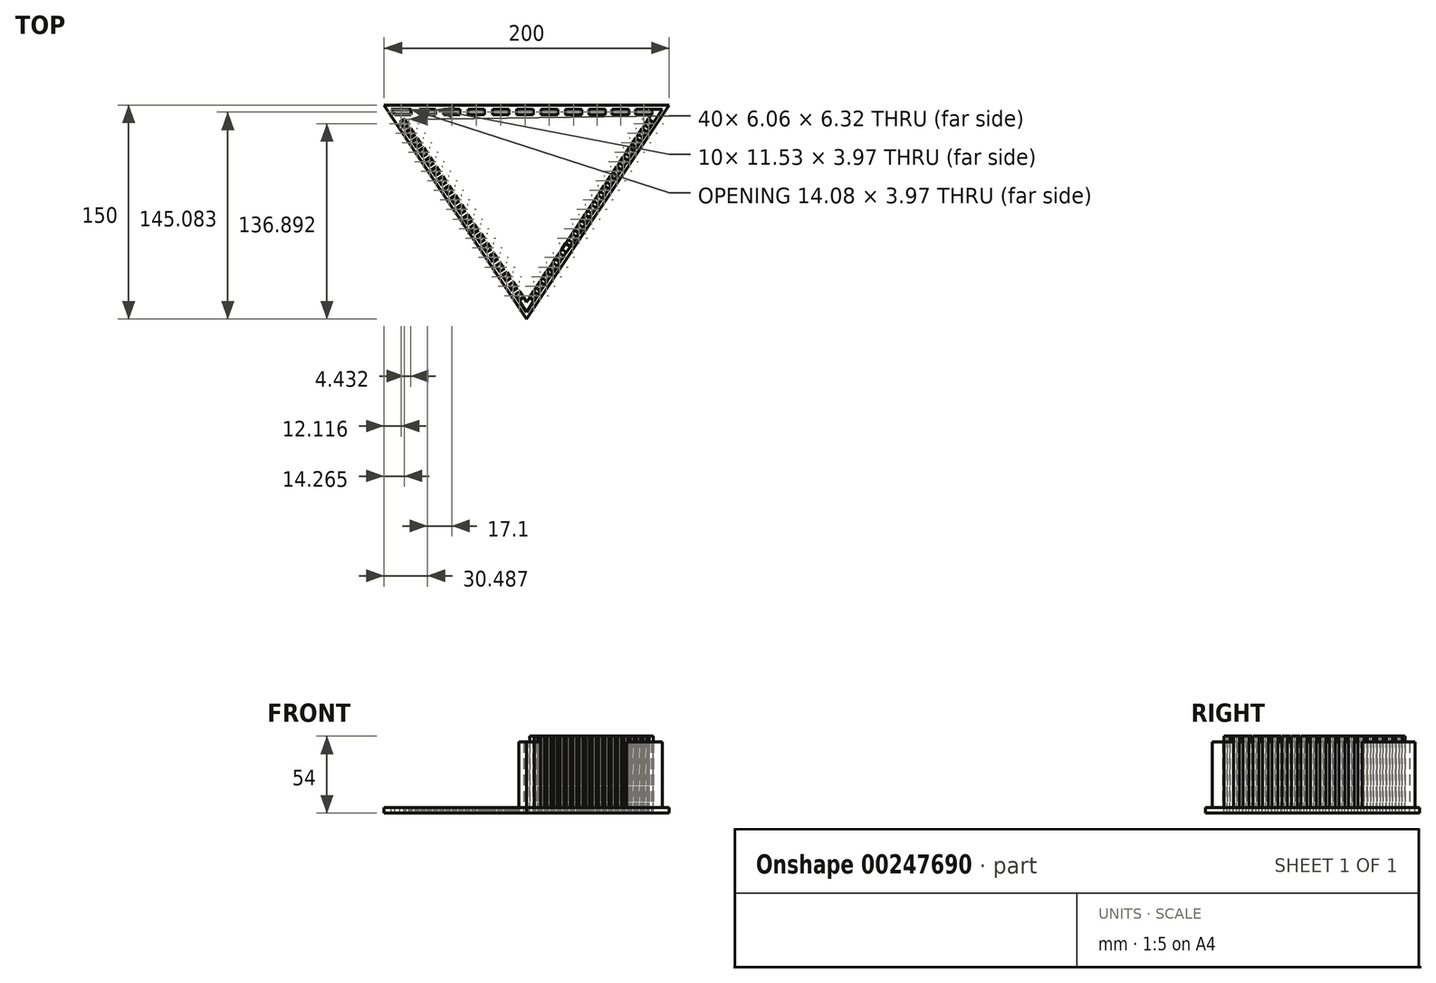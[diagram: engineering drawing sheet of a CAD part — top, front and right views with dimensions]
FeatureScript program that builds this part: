
annotation { "Feature Type Name" : "Feature", "Feature Type Description" : "" }
export const myFeature = defineFeature(function(context is Context, id is Id, definition is map)
    precondition{}
    {
        {
            var Q0;
            Q0=qCreatedBy(makeId("Top.planeOp"),FACE);
            var sketch = newSketch(context, id + "F0", { "sketchPlane" : qUnion([Q0])});
            skLineSegment(sketch, "E0.0", {"start": v(-75, 48.75) * mm, "end": v(125, 48.75) * mm});
            skLineSegment(sketch, "E0.1", {"start": v(125, 48.75) * mm, "end": v(25, -101.25) * mm});
            skLineSegment(sketch, "E0.2", {"start": v(25, -101.25) * mm, "end": v(-75, 48.75) * mm});
            skLineSegment(sketch, "E1.bottom", {"start": v(-75, 48.75) * mm, "end": v(-54.34, 48.75) * mm});
            skLineSegment(sketch, "E2.1.0.3", {"start": v(-49.2, 48.75) * mm, "end": v(-28.55, 48.75) * mm});
            skLineSegment(sketch, "E2.2.0.3", {"start": v(-23.42, 48.75) * mm, "end": v(-2.76, 48.75) * mm});
            skLineSegment(sketch, "E2.3.0.3", {"start": v(2.37, 48.75) * mm, "end": v(23.03, 48.75) * mm});
            skLineSegment(sketch, "E2.4.0.3", {"start": v(28.17, 48.75) * mm, "end": v(48.82, 48.75) * mm});
            skLineSegment(sketch, "E2.5.0.3", {"start": v(53.96, 48.75) * mm, "end": v(74.61, 48.75) * mm});
            skLineSegment(sketch, "E3.bottom", {"start": v(-67.38, 41.85) * mm, "end": v(-55.85, 41.85) * mm});
            skLineSegment(sketch, "E3.top", {"start": v(-67.38, 45.82) * mm, "end": v(-55.85, 45.82) * mm});
            skLineSegment(sketch, "E3.left", {"start": v(-67.38, 41.85) * mm, "end": v(-67.38, 45.82) * mm});
            skLineSegment(sketch, "E3.right", {"start": v(-55.85, 41.85) * mm, "end": v(-55.85, 45.82) * mm});
            skLineSegment(sketch, "E4.1.0.0", {"start": v(-50.28, 41.85) * mm, "end": v(-38.75, 41.85) * mm});
            skLineSegment(sketch, "E4.1.0.1", {"start": v(-38.75, 41.85) * mm, "end": v(-38.75, 45.82) * mm});
            skLineSegment(sketch, "E4.1.0.2", {"start": v(-50.28, 45.82) * mm, "end": v(-38.75, 45.82) * mm});
            skLineSegment(sketch, "E4.1.0.3", {"start": v(-50.28, 41.85) * mm, "end": v(-50.28, 45.82) * mm});
            skLineSegment(sketch, "E4.2.0.0", {"start": v(-33.18, 41.85) * mm, "end": v(-21.65, 41.85) * mm});
            skLineSegment(sketch, "E4.2.0.1", {"start": v(-21.65, 41.85) * mm, "end": v(-21.65, 45.82) * mm});
            skLineSegment(sketch, "E4.2.0.2", {"start": v(-33.18, 45.82) * mm, "end": v(-21.65, 45.82) * mm});
            skLineSegment(sketch, "E4.2.0.3", {"start": v(-33.18, 41.85) * mm, "end": v(-33.18, 45.82) * mm});
            skLineSegment(sketch, "E4.3.0.0", {"start": v(-16.08, 41.85) * mm, "end": v(-4.55, 41.85) * mm});
            skLineSegment(sketch, "E4.3.0.1", {"start": v(-4.55, 41.85) * mm, "end": v(-4.55, 45.82) * mm});
            skLineSegment(sketch, "E4.3.0.2", {"start": v(-16.08, 45.82) * mm, "end": v(-4.55, 45.82) * mm});
            skLineSegment(sketch, "E4.3.0.3", {"start": v(-16.08, 41.85) * mm, "end": v(-16.08, 45.82) * mm});
            skLineSegment(sketch, "E4.4.0.0", {"start": v(1.02, 41.85) * mm, "end": v(12.55, 41.85) * mm});
            skLineSegment(sketch, "E4.4.0.1", {"start": v(12.55, 41.85) * mm, "end": v(12.55, 45.82) * mm});
            skLineSegment(sketch, "E4.4.0.2", {"start": v(1.02, 45.82) * mm, "end": v(12.55, 45.82) * mm});
            skLineSegment(sketch, "E4.4.0.3", {"start": v(1.02, 41.85) * mm, "end": v(1.02, 45.82) * mm});
            skLineSegment(sketch, "E4.5.0.0", {"start": v(18.12, 41.85) * mm, "end": v(29.65, 41.85) * mm});
            skLineSegment(sketch, "E4.5.0.1", {"start": v(29.65, 41.85) * mm, "end": v(29.65, 45.82) * mm});
            skLineSegment(sketch, "E4.5.0.2", {"start": v(18.12, 45.82) * mm, "end": v(29.65, 45.82) * mm});
            skLineSegment(sketch, "E4.5.0.3", {"start": v(18.12, 41.85) * mm, "end": v(18.12, 45.82) * mm});
            skLineSegment(sketch, "E4.6.0.0", {"start": v(35.22, 41.85) * mm, "end": v(46.75, 41.85) * mm});
            skLineSegment(sketch, "E4.6.0.1", {"start": v(46.75, 41.85) * mm, "end": v(46.75, 45.82) * mm});
            skLineSegment(sketch, "E4.6.0.2", {"start": v(35.22, 45.82) * mm, "end": v(46.75, 45.82) * mm});
            skLineSegment(sketch, "E4.6.0.3", {"start": v(35.22, 41.85) * mm, "end": v(35.22, 45.82) * mm});
            skLineSegment(sketch, "E4.7.0.0", {"start": v(52.32, 41.85) * mm, "end": v(63.85, 41.85) * mm});
            skLineSegment(sketch, "E4.7.0.1", {"start": v(63.85, 41.85) * mm, "end": v(63.85, 45.82) * mm});
            skLineSegment(sketch, "E4.7.0.2", {"start": v(52.32, 45.82) * mm, "end": v(63.85, 45.82) * mm});
            skLineSegment(sketch, "E4.7.0.3", {"start": v(52.32, 41.85) * mm, "end": v(52.32, 45.82) * mm});
            skLineSegment(sketch, "E4.direction1", {"start": v(-67.38, 41.85) * mm, "end": v(-50.28, 41.85) * mm, "construction": true});
            skLineSegment(sketch, "E5", {"start": v(25, -101.25) * mm, "end": v(25, 48.75) * mm, "construction": true});
            skLineSegment(sketch, "E6.1.0.0", {"start": v(68.72, 41.85) * mm, "end": v(80.25, 41.85) * mm});
            skLineSegment(sketch, "E6.1.0.1", {"start": v(80.25, 41.85) * mm, "end": v(80.25, 45.82) * mm});
            skLineSegment(sketch, "E6.1.0.2", {"start": v(68.72, 45.82) * mm, "end": v(80.25, 45.82) * mm});
            skLineSegment(sketch, "E6.1.0.3", {"start": v(68.72, 41.85) * mm, "end": v(68.72, 45.82) * mm});
            skLineSegment(sketch, "E6.2.0.0", {"start": v(85.12, 41.85) * mm, "end": v(96.65, 41.85) * mm});
            skLineSegment(sketch, "E6.2.0.1", {"start": v(96.65, 41.85) * mm, "end": v(96.65, 45.82) * mm});
            skLineSegment(sketch, "E6.2.0.2", {"start": v(85.12, 45.82) * mm, "end": v(96.65, 45.82) * mm});
            skLineSegment(sketch, "E6.2.0.3", {"start": v(85.12, 41.85) * mm, "end": v(85.12, 45.82) * mm});
            skLineSegment(sketch, "E6.3.0.0", {"start": v(101.52, 41.85) * mm, "end": v(113.05, 41.85) * mm});
            skLineSegment(sketch, "E6.3.0.1", {"start": v(113.05, 41.85) * mm, "end": v(113.05, 45.82) * mm});
            skLineSegment(sketch, "E6.3.0.2", {"start": v(101.52, 45.82) * mm, "end": v(113.05, 45.82) * mm});
            skLineSegment(sketch, "E6.3.0.3", {"start": v(101.52, 41.85) * mm, "end": v(101.52, 45.82) * mm});
            skLineSegment(sketch, "E6.direction1", {"start": v(52.32, 41.85) * mm, "end": v(68.72, 41.85) * mm, "construction": true});
            skLineSegment(sketch, "E7.1", {"start": v(112.67, 42.15) * mm, "end": v(25, -89.35) * mm});
            skLineSegment(sketch, "E7.2", {"start": v(-62.67, 42.15) * mm, "end": v(112.67, 42.15) * mm});
            skLineSegment(sketch, "E8", {"start": v(-63.77, 36.58) * mm, "end": v(-60.44, 38.8) * mm});
            skLineSegment(sketch, "E9", {"start": v(-60.44, 38.8) * mm, "end": v(-57.7, 34.7) * mm});
            skLineSegment(sketch, "E10", {"start": v(-57.7, 34.7) * mm, "end": v(-61.03, 32.48) * mm});
            skLineSegment(sketch, "E11", {"start": v(-61.03, 32.48) * mm, "end": v(-63.77, 36.58) * mm});
            skLineSegment(sketch, "E12.1.0.0", {"start": v(-56.6, 25.8) * mm, "end": v(-59.33, 29.9) * mm});
            skLineSegment(sketch, "E12.1.0.1", {"start": v(-53.27, 28.02) * mm, "end": v(-56.6, 25.8) * mm});
            skLineSegment(sketch, "E12.1.0.2", {"start": v(-56, 32.12) * mm, "end": v(-53.27, 28.02) * mm});
            skLineSegment(sketch, "E12.1.0.3", {"start": v(-59.33, 29.9) * mm, "end": v(-56, 32.12) * mm});
            skLineSegment(sketch, "E12.2.0.0", {"start": v(-52.17, 19.12) * mm, "end": v(-54.9, 23.22) * mm});
            skLineSegment(sketch, "E12.2.0.1", {"start": v(-48.84, 21.34) * mm, "end": v(-52.17, 19.12) * mm});
            skLineSegment(sketch, "E12.2.0.2", {"start": v(-51.57, 25.44) * mm, "end": v(-48.84, 21.34) * mm});
            skLineSegment(sketch, "E12.2.0.3", {"start": v(-54.9, 23.22) * mm, "end": v(-51.57, 25.44) * mm});
            skLineSegment(sketch, "E12.3.0.0", {"start": v(-47.74, 12.43) * mm, "end": v(-50.47, 16.53) * mm});
            skLineSegment(sketch, "E12.3.0.1", {"start": v(-44.4, 14.65) * mm, "end": v(-47.74, 12.43) * mm});
            skLineSegment(sketch, "E12.3.0.2", {"start": v(-47.14, 18.75) * mm, "end": v(-44.4, 14.65) * mm});
            skLineSegment(sketch, "E12.3.0.3", {"start": v(-50.47, 16.53) * mm, "end": v(-47.14, 18.75) * mm});
            skLineSegment(sketch, "E12.4.0.0", {"start": v(-43.3, 5.75) * mm, "end": v(-46.04, 9.85) * mm});
            skLineSegment(sketch, "E12.4.0.1", {"start": v(-39.97, 7.97) * mm, "end": v(-43.3, 5.75) * mm});
            skLineSegment(sketch, "E12.4.0.2", {"start": v(-42.7, 12.07) * mm, "end": v(-39.97, 7.97) * mm});
            skLineSegment(sketch, "E12.4.0.3", {"start": v(-46.04, 9.85) * mm, "end": v(-42.7, 12.07) * mm});
            skLineSegment(sketch, "E12.5.0.0", {"start": v(-38.87, -0.93) * mm, "end": v(-41.6, 3.17) * mm});
            skLineSegment(sketch, "E12.5.0.1", {"start": v(-35.54, 1.29) * mm, "end": v(-38.87, -0.93) * mm});
            skLineSegment(sketch, "E12.5.0.2", {"start": v(-38.28, 5.39) * mm, "end": v(-35.54, 1.29) * mm});
            skLineSegment(sketch, "E12.5.0.3", {"start": v(-41.6, 3.17) * mm, "end": v(-38.28, 5.39) * mm});
            skLineSegment(sketch, "E12.6.0.0", {"start": v(-34.44, -7.61) * mm, "end": v(-37.17, -3.51) * mm});
            skLineSegment(sketch, "E12.6.0.1", {"start": v(-31.1, -5.4) * mm, "end": v(-34.44, -7.61) * mm});
            skLineSegment(sketch, "E12.6.0.2", {"start": v(-33.84, -1.3) * mm, "end": v(-31.1, -5.4) * mm});
            skLineSegment(sketch, "E12.6.0.3", {"start": v(-37.17, -3.51) * mm, "end": v(-33.84, -1.3) * mm});
            skLineSegment(sketch, "E12.7.0.0", {"start": v(-30, -14.3) * mm, "end": v(-32.74, -10.2) * mm});
            skLineSegment(sketch, "E12.7.0.1", {"start": v(-26.68, -12.08) * mm, "end": v(-30, -14.3) * mm});
            skLineSegment(sketch, "E12.7.0.2", {"start": v(-29.41, -7.98) * mm, "end": v(-26.68, -12.08) * mm});
            skLineSegment(sketch, "E12.7.0.3", {"start": v(-32.74, -10.2) * mm, "end": v(-29.41, -7.98) * mm});
            skLineSegment(sketch, "E12.8.0.0", {"start": v(-25.57, -20.98) * mm, "end": v(-28.3, -16.88) * mm});
            skLineSegment(sketch, "E12.8.0.1", {"start": v(-22.25, -18.76) * mm, "end": v(-25.57, -20.98) * mm});
            skLineSegment(sketch, "E12.8.0.2", {"start": v(-24.98, -14.66) * mm, "end": v(-22.25, -18.76) * mm});
            skLineSegment(sketch, "E12.8.0.3", {"start": v(-28.3, -16.88) * mm, "end": v(-24.98, -14.66) * mm});
            skLineSegment(sketch, "E12.9.0.0", {"start": v(-21.14, -27.66) * mm, "end": v(-23.87, -23.56) * mm});
            skLineSegment(sketch, "E12.9.0.1", {"start": v(-17.81, -25.44) * mm, "end": v(-21.14, -27.66) * mm});
            skLineSegment(sketch, "E12.9.0.2", {"start": v(-20.55, -21.34) * mm, "end": v(-17.81, -25.44) * mm});
            skLineSegment(sketch, "E12.9.0.3", {"start": v(-23.87, -23.56) * mm, "end": v(-20.55, -21.34) * mm});
            skLineSegment(sketch, "E12.direction1", {"start": v(-61.03, 32.48) * mm, "end": v(-56.6, 25.8) * mm, "construction": true});
            skLineSegment(sketch, "E13.1.0.0", {"start": v(-13.27, -32.18) * mm, "end": v(-16.6, -34.4) * mm});
            skLineSegment(sketch, "E13.1.0.1", {"start": v(-16.6, -34.4) * mm, "end": v(-19.33, -30.3) * mm});
            skLineSegment(sketch, "E13.1.0.2", {"start": v(-16, -28.08) * mm, "end": v(-13.27, -32.18) * mm});
            skLineSegment(sketch, "E13.1.0.3", {"start": v(-19.33, -30.3) * mm, "end": v(-16, -28.08) * mm});
            skLineSegment(sketch, "E13.2.0.0", {"start": v(-8.73, -38.92) * mm, "end": v(-12.06, -41.14) * mm});
            skLineSegment(sketch, "E13.2.0.1", {"start": v(-12.06, -41.14) * mm, "end": v(-14.8, -37.04) * mm});
            skLineSegment(sketch, "E13.2.0.2", {"start": v(-11.46, -34.82) * mm, "end": v(-8.73, -38.92) * mm});
            skLineSegment(sketch, "E13.2.0.3", {"start": v(-14.8, -37.04) * mm, "end": v(-11.46, -34.82) * mm});
            skLineSegment(sketch, "E13.3.0.0", {"start": v(-4.19, -45.66) * mm, "end": v(-7.52, -47.87) * mm});
            skLineSegment(sketch, "E13.3.0.1", {"start": v(-7.52, -47.87) * mm, "end": v(-10.25, -43.77) * mm});
            skLineSegment(sketch, "E13.3.0.2", {"start": v(-6.92, -41.56) * mm, "end": v(-4.19, -45.66) * mm});
            skLineSegment(sketch, "E13.3.0.3", {"start": v(-10.25, -43.77) * mm, "end": v(-6.92, -41.56) * mm});
            skLineSegment(sketch, "E13.4.0.0", {"start": v(0.35, -52.4) * mm, "end": v(-2.98, -54.61) * mm});
            skLineSegment(sketch, "E13.4.0.1", {"start": v(-2.98, -54.61) * mm, "end": v(-5.71, -50.51) * mm});
            skLineSegment(sketch, "E13.4.0.2", {"start": v(-2.38, -48.3) * mm, "end": v(0.35, -52.4) * mm});
            skLineSegment(sketch, "E13.4.0.3", {"start": v(-5.71, -50.51) * mm, "end": v(-2.38, -48.3) * mm});
            skLineSegment(sketch, "E13.5.0.0", {"start": v(4.9, -59.13) * mm, "end": v(1.56, -61.35) * mm});
            skLineSegment(sketch, "E13.5.0.1", {"start": v(1.56, -61.35) * mm, "end": v(-1.17, -57.25) * mm});
            skLineSegment(sketch, "E13.5.0.2", {"start": v(2.16, -55.03) * mm, "end": v(4.9, -59.13) * mm});
            skLineSegment(sketch, "E13.5.0.3", {"start": v(-1.17, -57.25) * mm, "end": v(2.16, -55.03) * mm});
            skLineSegment(sketch, "E13.6.0.0", {"start": v(9.43, -65.87) * mm, "end": v(6.1, -68.09) * mm});
            skLineSegment(sketch, "E13.6.0.1", {"start": v(6.1, -68.09) * mm, "end": v(3.37, -63.99) * mm});
            skLineSegment(sketch, "E13.6.0.2", {"start": v(6.7, -61.77) * mm, "end": v(9.43, -65.87) * mm});
            skLineSegment(sketch, "E13.6.0.3", {"start": v(3.37, -63.99) * mm, "end": v(6.7, -61.77) * mm});
            skLineSegment(sketch, "E13.7.0.0", {"start": v(13.97, -72.6) * mm, "end": v(10.65, -74.82) * mm});
            skLineSegment(sketch, "E13.7.0.1", {"start": v(10.65, -74.82) * mm, "end": v(7.91, -70.72) * mm});
            skLineSegment(sketch, "E13.7.0.2", {"start": v(11.24, -68.5) * mm, "end": v(13.97, -72.6) * mm});
            skLineSegment(sketch, "E13.7.0.3", {"start": v(7.91, -70.72) * mm, "end": v(11.24, -68.5) * mm});
            skLineSegment(sketch, "E13.8.0.0", {"start": v(18.51, -79.34) * mm, "end": v(15.19, -81.56) * mm});
            skLineSegment(sketch, "E13.8.0.1", {"start": v(15.19, -81.56) * mm, "end": v(12.45, -77.46) * mm});
            skLineSegment(sketch, "E13.8.0.2", {"start": v(15.78, -75.24) * mm, "end": v(18.51, -79.34) * mm});
            skLineSegment(sketch, "E13.8.0.3", {"start": v(12.45, -77.46) * mm, "end": v(15.78, -75.24) * mm});
            skLineSegment(sketch, "E13.9.0.0", {"start": v(23.06, -86.08) * mm, "end": v(19.73, -88.3) * mm});
            skLineSegment(sketch, "E13.9.0.1", {"start": v(19.73, -88.3) * mm, "end": v(17, -84.2) * mm});
            skLineSegment(sketch, "E13.9.0.2", {"start": v(20.32, -81.98) * mm, "end": v(23.06, -86.08) * mm});
            skLineSegment(sketch, "E13.9.0.3", {"start": v(17, -84.2) * mm, "end": v(20.32, -81.98) * mm});
            skLineSegment(sketch, "E13.direction1", {"start": v(-21.14, -27.66) * mm, "end": v(-16.6, -34.4) * mm, "construction": true});
            skLineSegment(sketch, "E14.MirrorCS", {"start": v(26.94, -86.08) * mm, "end": v(30.27, -88.3) * mm});
            skLineSegment(sketch, "E15.MirrorCS", {"start": v(29.68, -81.98) * mm, "end": v(26.94, -86.08) * mm});
            skLineSegment(sketch, "E16.MirrorCS", {"start": v(33, -84.2) * mm, "end": v(29.68, -81.98) * mm});
            skLineSegment(sketch, "E17.MirrorCS", {"start": v(30.27, -88.3) * mm, "end": v(33, -84.2) * mm});
            skLineSegment(sketch, "E18.MirrorCS", {"start": v(34.22, -75.24) * mm, "end": v(31.49, -79.34) * mm});
            skLineSegment(sketch, "E19.MirrorCS", {"start": v(31.49, -79.34) * mm, "end": v(34.81, -81.56) * mm});
            skLineSegment(sketch, "E20.MirrorCS", {"start": v(34.81, -81.56) * mm, "end": v(37.55, -77.46) * mm});
            skLineSegment(sketch, "E21.MirrorCS", {"start": v(37.55, -77.46) * mm, "end": v(34.22, -75.24) * mm});
            skLineSegment(sketch, "E22.MirrorCS", {"start": v(36.03, -72.6) * mm, "end": v(39.35, -74.82) * mm});
            skLineSegment(sketch, "E23.MirrorCS", {"start": v(38.76, -68.5) * mm, "end": v(36.03, -72.6) * mm});
            skLineSegment(sketch, "E24.MirrorCS", {"start": v(42.09, -70.72) * mm, "end": v(38.76, -68.5) * mm});
            skLineSegment(sketch, "E25.MirrorCS", {"start": v(39.35, -74.82) * mm, "end": v(42.09, -70.72) * mm});
            skLineSegment(sketch, "E26.MirrorCS", {"start": v(40.57, -65.87) * mm, "end": v(43.9, -68.09) * mm});
            skLineSegment(sketch, "E27.MirrorCS", {"start": v(43.9, -68.09) * mm, "end": v(46.63, -63.99) * mm});
            skLineSegment(sketch, "E28.MirrorCS", {"start": v(46.63, -63.99) * mm, "end": v(43.3, -61.77) * mm});
            skLineSegment(sketch, "E29.MirrorCS", {"start": v(43.3, -61.77) * mm, "end": v(40.57, -65.87) * mm});
            skLineSegment(sketch, "E30.MirrorCS", {"start": v(45.1, -59.13) * mm, "end": v(48.44, -61.35) * mm});
            skLineSegment(sketch, "E31.MirrorCS", {"start": v(48.44, -61.35) * mm, "end": v(51.17, -57.25) * mm});
            skLineSegment(sketch, "E32.MirrorCS", {"start": v(51.17, -57.25) * mm, "end": v(47.84, -55.03) * mm});
            skLineSegment(sketch, "E33.MirrorCS", {"start": v(25, -89.35) * mm, "end": v(112.67, 42.15) * mm});
            skLineSegment(sketch, "E34.MirrorCS", {"start": v(47.84, -55.03) * mm, "end": v(45.1, -59.13) * mm});
            skLineSegment(sketch, "E35.MirrorCS", {"start": v(49.65, -52.4) * mm, "end": v(52.98, -54.61) * mm});
            skLineSegment(sketch, "E36.MirrorCS", {"start": v(55.71, -50.51) * mm, "end": v(52.38, -48.3) * mm});
            skLineSegment(sketch, "E37.MirrorCS", {"start": v(52.38, -48.3) * mm, "end": v(49.65, -52.4) * mm});
            skLineSegment(sketch, "E38.MirrorCS", {"start": v(54.19, -45.66) * mm, "end": v(57.52, -47.87) * mm});
            skLineSegment(sketch, "E39.MirrorCS", {"start": v(57.52, -47.87) * mm, "end": v(60.25, -43.77) * mm});
            skLineSegment(sketch, "E40.MirrorCS", {"start": v(60.25, -43.77) * mm, "end": v(56.92, -41.56) * mm});
            skLineSegment(sketch, "E41.MirrorCS", {"start": v(56.92, -41.56) * mm, "end": v(54.19, -45.66) * mm});
            skLineSegment(sketch, "E42.MirrorCS", {"start": v(58.73, -38.92) * mm, "end": v(62.06, -41.14) * mm});
            skLineSegment(sketch, "E43.MirrorCS", {"start": v(62.06, -41.14) * mm, "end": v(64.8, -37.04) * mm});
            skLineSegment(sketch, "E44.MirrorCS", {"start": v(61.46, -34.82) * mm, "end": v(58.73, -38.92) * mm});
            skLineSegment(sketch, "E45.MirrorCS", {"start": v(64.8, -37.04) * mm, "end": v(61.46, -34.82) * mm});
            skLineSegment(sketch, "E46.MirrorCS", {"start": v(73.87, -23.56) * mm, "end": v(70.55, -21.34) * mm});
            skLineSegment(sketch, "E47.MirrorCS", {"start": v(69.33, -30.3) * mm, "end": v(66, -28.08) * mm});
            skLineSegment(sketch, "E48.MirrorCS", {"start": v(63.27, -32.18) * mm, "end": v(66.6, -34.4) * mm});
            skLineSegment(sketch, "E49.MirrorCS", {"start": v(71.14, -27.66) * mm, "end": v(66.6, -34.4) * mm, "construction": true});
            skLineSegment(sketch, "E50.MirrorCS", {"start": v(66.6, -34.4) * mm, "end": v(69.33, -30.3) * mm});
            skLineSegment(sketch, "E51.MirrorCS", {"start": v(66, -28.08) * mm, "end": v(63.27, -32.18) * mm});
            skLineSegment(sketch, "E52.MirrorCS", {"start": v(70.55, -21.34) * mm, "end": v(67.81, -25.44) * mm});
            skLineSegment(sketch, "E53.MirrorCS", {"start": v(71.14, -27.66) * mm, "end": v(73.87, -23.56) * mm});
            skLineSegment(sketch, "E54.MirrorCS", {"start": v(72.25, -18.76) * mm, "end": v(75.57, -20.98) * mm});
            skLineSegment(sketch, "E55.MirrorCS", {"start": v(75.57, -20.98) * mm, "end": v(78.3, -16.88) * mm});
            skLineSegment(sketch, "E56.MirrorCS", {"start": v(74.98, -14.66) * mm, "end": v(72.25, -18.76) * mm});
            skLineSegment(sketch, "E57.MirrorCS", {"start": v(78.3, -16.88) * mm, "end": v(74.98, -14.66) * mm});
            skLineSegment(sketch, "E58.MirrorCS", {"start": v(76.68, -12.08) * mm, "end": v(80, -14.3) * mm});
            skLineSegment(sketch, "E59.MirrorCS", {"start": v(80, -14.3) * mm, "end": v(82.74, -10.2) * mm});
            skLineSegment(sketch, "E60.MirrorCS", {"start": v(79.41, -7.98) * mm, "end": v(76.68, -12.08) * mm});
            skLineSegment(sketch, "E61.MirrorCS", {"start": v(82.74, -10.2) * mm, "end": v(79.41, -7.98) * mm});
            skLineSegment(sketch, "E62.MirrorCS", {"start": v(81.1, -5.4) * mm, "end": v(84.44, -7.61) * mm});
            skLineSegment(sketch, "E63.MirrorCS", {"start": v(84.44, -7.61) * mm, "end": v(87.17, -3.51) * mm});
            skLineSegment(sketch, "E64.MirrorCS", {"start": v(83.84, -1.3) * mm, "end": v(81.1, -5.4) * mm});
            skLineSegment(sketch, "E65.MirrorCS", {"start": v(87.17, -3.51) * mm, "end": v(83.84, -1.3) * mm});
            skLineSegment(sketch, "E66.MirrorCS", {"start": v(85.54, 1.29) * mm, "end": v(88.87, -0.93) * mm});
            skLineSegment(sketch, "E67.MirrorCS", {"start": v(88.87, -0.93) * mm, "end": v(91.6, 3.17) * mm});
            skLineSegment(sketch, "E68.MirrorCS", {"start": v(88.28, 5.39) * mm, "end": v(85.54, 1.29) * mm});
            skLineSegment(sketch, "E69.MirrorCS", {"start": v(91.6, 3.17) * mm, "end": v(88.28, 5.39) * mm});
            skLineSegment(sketch, "E70.MirrorCS", {"start": v(89.97, 7.97) * mm, "end": v(93.3, 5.75) * mm});
            skLineSegment(sketch, "E71.MirrorCS", {"start": v(93.3, 5.75) * mm, "end": v(96.04, 9.85) * mm});
            skLineSegment(sketch, "E72.MirrorCS", {"start": v(92.7, 12.07) * mm, "end": v(89.97, 7.97) * mm});
            skLineSegment(sketch, "E73.MirrorCS", {"start": v(96.04, 9.85) * mm, "end": v(92.7, 12.07) * mm});
            skLineSegment(sketch, "E74.MirrorCS", {"start": v(94.4, 14.65) * mm, "end": v(97.74, 12.43) * mm});
            skLineSegment(sketch, "E75.MirrorCS", {"start": v(97.74, 12.43) * mm, "end": v(100.47, 16.53) * mm});
            skLineSegment(sketch, "E76.MirrorCS", {"start": v(100.47, 16.53) * mm, "end": v(97.14, 18.75) * mm});
            skLineSegment(sketch, "E77.MirrorCS", {"start": v(97.14, 18.75) * mm, "end": v(94.4, 14.65) * mm});
            skLineSegment(sketch, "E78.MirrorCS", {"start": v(98.84, 21.34) * mm, "end": v(102.17, 19.12) * mm});
            skLineSegment(sketch, "E79.MirrorCS", {"start": v(102.17, 19.12) * mm, "end": v(104.9, 23.22) * mm});
            skLineSegment(sketch, "E80.MirrorCS", {"start": v(101.57, 25.44) * mm, "end": v(98.84, 21.34) * mm});
            skLineSegment(sketch, "E81.MirrorCS", {"start": v(104.9, 23.22) * mm, "end": v(101.57, 25.44) * mm});
            skLineSegment(sketch, "E82.MirrorCS", {"start": v(103.27, 28.02) * mm, "end": v(106.6, 25.8) * mm});
            skLineSegment(sketch, "E83.MirrorCS", {"start": v(106, 32.12) * mm, "end": v(103.27, 28.02) * mm});
            skLineSegment(sketch, "E84.MirrorCS", {"start": v(106.6, 25.8) * mm, "end": v(109.33, 29.9) * mm});
            skLineSegment(sketch, "E85.MirrorCS", {"start": v(109.33, 29.9) * mm, "end": v(106, 32.12) * mm});
            skLineSegment(sketch, "E86.MirrorCS", {"start": v(107.7, 34.7) * mm, "end": v(111.03, 32.48) * mm});
            skLineSegment(sketch, "E87.MirrorCS", {"start": v(111.03, 32.48) * mm, "end": v(106.6, 25.8) * mm, "construction": true});
            skLineSegment(sketch, "E88.MirrorCS", {"start": v(113.77, 36.58) * mm, "end": v(110.44, 38.8) * mm});
            skLineSegment(sketch, "E89", {"start": v(71.14, -27.66) * mm, "end": v(67.81, -25.44) * mm});
            skLineSegment(sketch, "E90", {"start": v(113.05, 45.82) * mm, "end": v(120.14, 45.82) * mm});
            skLineSegment(sketch, "E91", {"start": v(120.14, 45.82) * mm, "end": v(-69.92, 45.82) * mm});
            skLineSegment(sketch, "E92", {"start": v(19.73, -88.3) * mm, "end": v(25, -96.57) * mm});
            skLineSegment(sketch, "E93", {"start": v(17, -84.2) * mm, "end": v(15.19, -81.56) * mm});
            skLineSegment(sketch, "E94", {"start": v(12.45, -77.46) * mm, "end": v(10.65, -74.82) * mm});
            skLineSegment(sketch, "E95", {"start": v(7.91, -70.72) * mm, "end": v(6.1, -68.09) * mm});
            skLineSegment(sketch, "E96", {"start": v(3.37, -63.99) * mm, "end": v(1.56, -61.35) * mm});
            skLineSegment(sketch, "E97", {"start": v(-1.17, -57.25) * mm, "end": v(-2.98, -54.61) * mm});
            skLineSegment(sketch, "E98", {"start": v(-5.71, -50.51) * mm, "end": v(-7.52, -47.87) * mm});
            skLineSegment(sketch, "E99", {"start": v(-10.25, -43.77) * mm, "end": v(-12.06, -41.14) * mm});
            skLineSegment(sketch, "E100", {"start": v(-14.8, -37.04) * mm, "end": v(-16.6, -34.4) * mm});
            skLineSegment(sketch, "E101", {"start": v(-19.33, -30.3) * mm, "end": v(-21.14, -27.66) * mm});
            skLineSegment(sketch, "E102", {"start": v(-23.97, -23.57) * mm, "end": v(-38.87, -0.93) * mm});
            skLineSegment(sketch, "E103", {"start": v(-41.6, 3.17) * mm, "end": v(-69.92, 45.82) * mm});
            skLineSegment(sketch, "E104", {"start": v(111.03, 32.48) * mm, "end": v(113.77, 36.58) * mm});
            skLineSegment(sketch, "E105", {"start": v(120.14, 45.82) * mm, "end": v(30.27, -88.3) * mm});
            skLineSegment(sketch, "E106", {"start": v(30.27, -88.3) * mm, "end": v(25, -96.57) * mm});
            skLineSegment(sketch, "E107", {"start": v(25, -89.35) * mm, "end": v(23.06, -86.08) * mm});
            skLineSegment(sketch, "E108", {"start": v(20.32, -81.98) * mm, "end": v(18.51, -79.34) * mm});
            skLineSegment(sketch, "E109", {"start": v(15.78, -75.24) * mm, "end": v(13.97, -72.6) * mm});
            skLineSegment(sketch, "E110", {"start": v(11.24, -68.5) * mm, "end": v(9.43, -65.87) * mm});
            skLineSegment(sketch, "E111", {"start": v(6.7, -61.7) * mm, "end": v(4.9, -59.13) * mm});
            skLineSegment(sketch, "E112", {"start": v(2.16, -55.03) * mm, "end": v(0.35, -52.4) * mm});
            skLineSegment(sketch, "E113", {"start": v(-2.38, -48.3) * mm, "end": v(-4.19, -45.66) * mm});
            skSolve(sketch);
        }
        {
            var Q0;
            {var subQ123=sQuery(id+"F0.wireOp",EDGE,"E0.1");Q0=makeQuery(id+"F0.imprint","IMPRINT",FACE,{"disambiguationData":[TD([[makeQuery(id+"F0.imprint","IMPRINT",EDGE,{"derivedFrom":subQ123}),-1.0]])]});}
            var Q1;
            {var subQ52=sQuery(id+"F0.wireOp",EDGE,"E10");Q1=makeQuery(id+"F0.imprint","IMPRINT",FACE,{"disambiguationData":[TD([[makeQuery(id+"F0.imprint","IMPRINT",EDGE,{"derivedFrom":subQ52}),1.0]])]});}
            var Q2;
            {var subQ49=sQuery(id+"F0.wireOp",EDGE,"E3.top");Q2=makeQuery(id+"F0.imprint","IMPRINT",FACE,{"disambiguationData":[TD([[makeQuery(id+"F0.imprint","IMPRINT",EDGE,{"derivedFrom":subQ49}),1.0]])]});}
            var Q3;
            {var subQ0=sQuery(id+"F0.wireOp",EDGE,"E17.MirrorCS");Q3=makeQuery(id+"F0.imprint","IMPRINT",FACE,{"disambiguationData":[TD([[makeQuery(id+"F0.imprint","IMPRINT",EDGE,{"derivedFrom":subQ0}),-1.0]])]});}
            var Q4;
            {var subQ6=sQuery(id+"F0.wireOp",EDGE,"E92");Q4=makeQuery(id+"F0.imprint","IMPRINT",FACE,{"disambiguationData":[TD([[makeQuery(id+"F0.imprint","IMPRINT",EDGE,{"derivedFrom":subQ6}),1.0]])]});}
            var Q5;
            {var subQ5=sQuery(id+"F0.wireOp",EDGE,"E93");Q5=makeQuery(id+"F0.imprint","IMPRINT",FACE,{"disambiguationData":[TD([[makeQuery(id+"F0.imprint","IMPRINT",EDGE,{"derivedFrom":subQ5}),-1.0]])]});}
            var Q6;
            {var subQ5=sQuery(id+"F0.wireOp",EDGE,"E94");Q6=makeQuery(id+"F0.imprint","IMPRINT",FACE,{"disambiguationData":[TD([[makeQuery(id+"F0.imprint","IMPRINT",EDGE,{"derivedFrom":subQ5}),-1.0]])]});}
            var Q7;
            {var subQ5=sQuery(id+"F0.wireOp",EDGE,"E95");Q7=makeQuery(id+"F0.imprint","IMPRINT",FACE,{"disambiguationData":[TD([[makeQuery(id+"F0.imprint","IMPRINT",EDGE,{"derivedFrom":subQ5}),-1.0]])]});}
            var Q8;
            {var subQ5=sQuery(id+"F0.wireOp",EDGE,"E96");Q8=makeQuery(id+"F0.imprint","IMPRINT",FACE,{"disambiguationData":[TD([[makeQuery(id+"F0.imprint","IMPRINT",EDGE,{"derivedFrom":subQ5}),-1.0]])]});}
            var Q9;
            {var subQ0=sQuery(id+"F0.wireOp",EDGE,"E105");var subQ1=sQuery(id+"F0.wireOp",EDGE,"E21.MirrorCS");var subQ2=makeQuery(id+"F0.imprint","INTERSECT",VERTEX,{"derivedFrom":[subQ1,subQ0]});Q9=makeQuery(id+"F0.imprint","IMPRINT",FACE,{"disambiguationData":[TD([[makeQuery(id+"F0.imprint","IMPRINT",EDGE,{"disambiguationData":[TD([[subQ2,-1.0]])],"derivedFrom":subQ1}),-1.0]])]});}
            var Q10;
            {var subQ0=sQuery(id+"F0.wireOp",EDGE,"E105");var subQ1=sQuery(id+"F0.wireOp",EDGE,"E24.MirrorCS");var subQ2=makeQuery(id+"F0.imprint","INTERSECT",VERTEX,{"derivedFrom":[subQ1,subQ0]});Q10=makeQuery(id+"F0.imprint","IMPRINT",FACE,{"disambiguationData":[TD([[makeQuery(id+"F0.imprint","IMPRINT",EDGE,{"disambiguationData":[TD([[subQ2,-1.0]])],"derivedFrom":subQ1}),-1.0]])]});}
            var Q11;
            {var subQ0=sQuery(id+"F0.wireOp",EDGE,"E105");var subQ1=sQuery(id+"F0.wireOp",EDGE,"E28.MirrorCS");var subQ2=makeQuery(id+"F0.imprint","INTERSECT",VERTEX,{"derivedFrom":[subQ1,subQ0]});Q11=makeQuery(id+"F0.imprint","IMPRINT",FACE,{"disambiguationData":[TD([[makeQuery(id+"F0.imprint","IMPRINT",EDGE,{"disambiguationData":[TD([[subQ2,-1.0]])],"derivedFrom":subQ1}),-1.0]])]});}
            var Q12;
            {var subQ30=sQuery(id+"F0.wireOp",EDGE,"E6.3.0.1");Q12=makeQuery(id+"F0.imprint","IMPRINT",FACE,{"disambiguationData":[TD([[makeQuery(id+"F0.imprint","IMPRINT",EDGE,{"derivedFrom":subQ30}),-1.0]])]});}
            var Q13;
            {var subQ0=sQuery(id+"F0.wireOp",EDGE,"E91");var subQ1=sQuery(id+"F0.wireOp",EDGE,"E4.4.0.1");var subQ2=makeQuery(id+"F0.imprint","INTERSECT",VERTEX,{"derivedFrom":[subQ1,subQ0]});Q13=makeQuery(id+"F0.imprint","IMPRINT",FACE,{"disambiguationData":[TD([[makeQuery(id+"F0.imprint","IMPRINT",EDGE,{"disambiguationData":[TD([[subQ2,1.0]])],"derivedFrom":subQ1}),-1.0]])]});}
            var Q14;
            {var subQ0=sQuery(id+"F0.wireOp",EDGE,"E91");var subQ1=sQuery(id+"F0.wireOp",EDGE,"E4.3.0.1");var subQ2=makeQuery(id+"F0.imprint","INTERSECT",VERTEX,{"derivedFrom":[subQ1,subQ0]});Q14=makeQuery(id+"F0.imprint","IMPRINT",FACE,{"disambiguationData":[TD([[makeQuery(id+"F0.imprint","IMPRINT",EDGE,{"disambiguationData":[TD([[subQ2,1.0]])],"derivedFrom":subQ1}),-1.0]])]});}
            var Q15;
            {var subQ0=sQuery(id+"F0.wireOp",EDGE,"E91");var subQ1=sQuery(id+"F0.wireOp",EDGE,"E4.1.0.1");var subQ2=makeQuery(id+"F0.imprint","INTERSECT",VERTEX,{"derivedFrom":[subQ1,subQ0]});Q15=makeQuery(id+"F0.imprint","IMPRINT",FACE,{"disambiguationData":[TD([[makeQuery(id+"F0.imprint","IMPRINT",EDGE,{"disambiguationData":[TD([[subQ2,1.0]])],"derivedFrom":subQ1}),-1.0]])]});}
            var Q16;
            {var subQ0=sQuery(id+"F0.wireOp",EDGE,"E91");var subQ1=sQuery(id+"F0.wireOp",EDGE,"E3.right");var subQ2=makeQuery(id+"F0.imprint","INTERSECT",VERTEX,{"derivedFrom":[subQ1,subQ0]});Q16=makeQuery(id+"F0.imprint","IMPRINT",FACE,{"disambiguationData":[TD([[makeQuery(id+"F0.imprint","IMPRINT",EDGE,{"disambiguationData":[TD([[subQ2,1.0]])],"derivedFrom":subQ1}),-1.0]])]});}
            var Q17;
            {var subQ0=sQuery(id+"F0.wireOp",EDGE,"E91");var subQ1=sQuery(id+"F0.wireOp",EDGE,"E4.2.0.1");var subQ2=makeQuery(id+"F0.imprint","INTERSECT",VERTEX,{"derivedFrom":[subQ1,subQ0]});Q17=makeQuery(id+"F0.imprint","IMPRINT",FACE,{"disambiguationData":[TD([[makeQuery(id+"F0.imprint","IMPRINT",EDGE,{"disambiguationData":[TD([[subQ2,1.0]])],"derivedFrom":subQ1}),-1.0]])]});}
            var Q18;
            {var subQ0=sQuery(id+"F0.wireOp",EDGE,"E91");var subQ1=sQuery(id+"F0.wireOp",EDGE,"E4.5.0.1");var subQ2=makeQuery(id+"F0.imprint","INTERSECT",VERTEX,{"derivedFrom":[subQ1,subQ0]});Q18=makeQuery(id+"F0.imprint","IMPRINT",FACE,{"disambiguationData":[TD([[makeQuery(id+"F0.imprint","IMPRINT",EDGE,{"disambiguationData":[TD([[subQ2,1.0]])],"derivedFrom":subQ1}),-1.0]])]});}
            var Q19;
            {var subQ0=sQuery(id+"F0.wireOp",EDGE,"E91");var subQ1=sQuery(id+"F0.wireOp",EDGE,"E4.6.0.1");var subQ2=makeQuery(id+"F0.imprint","INTERSECT",VERTEX,{"derivedFrom":[subQ1,subQ0]});Q19=makeQuery(id+"F0.imprint","IMPRINT",FACE,{"disambiguationData":[TD([[makeQuery(id+"F0.imprint","IMPRINT",EDGE,{"disambiguationData":[TD([[subQ2,1.0]])],"derivedFrom":subQ1}),-1.0]])]});}
            var Q20;
            {var subQ0=sQuery(id+"F0.wireOp",EDGE,"E91");var subQ1=sQuery(id+"F0.wireOp",EDGE,"E4.7.0.1");var subQ2=makeQuery(id+"F0.imprint","INTERSECT",VERTEX,{"derivedFrom":[subQ1,subQ0]});Q20=makeQuery(id+"F0.imprint","IMPRINT",FACE,{"disambiguationData":[TD([[makeQuery(id+"F0.imprint","IMPRINT",EDGE,{"disambiguationData":[TD([[subQ2,1.0]])],"derivedFrom":subQ1}),-1.0]])]});}
            var Q21;
            {var subQ0=sQuery(id+"F0.wireOp",EDGE,"E91");var subQ1=sQuery(id+"F0.wireOp",EDGE,"E6.1.0.1");var subQ2=makeQuery(id+"F0.imprint","INTERSECT",VERTEX,{"derivedFrom":[subQ1,subQ0]});Q21=makeQuery(id+"F0.imprint","IMPRINT",FACE,{"disambiguationData":[TD([[makeQuery(id+"F0.imprint","IMPRINT",EDGE,{"disambiguationData":[TD([[subQ2,1.0]])],"derivedFrom":subQ1}),-1.0]])]});}
            var Q22;
            {var subQ0=sQuery(id+"F0.wireOp",EDGE,"E91");var subQ1=sQuery(id+"F0.wireOp",EDGE,"E6.2.0.1");var subQ2=makeQuery(id+"F0.imprint","INTERSECT",VERTEX,{"derivedFrom":[subQ1,subQ0]});Q22=makeQuery(id+"F0.imprint","IMPRINT",FACE,{"disambiguationData":[TD([[makeQuery(id+"F0.imprint","IMPRINT",EDGE,{"disambiguationData":[TD([[subQ2,1.0]])],"derivedFrom":subQ1}),-1.0]])]});}
            var Q23;
            Q23=makeQuery(id+"F0.imprint","IMPRINT",FACE,{"disambiguationData":[TD([[makeQuery(id+"F0.imprint","IMPRINT",EDGE,{"derivedFrom":sQuery(id+"F0.wireOp",EDGE,"E13.4.0.0")}),1.0]])]});
            var Q24;
            Q24=makeQuery(id+"F0.imprint","IMPRINT",FACE,{"disambiguationData":[TD([[makeQuery(id+"F0.imprint","IMPRINT",EDGE,{"derivedFrom":sQuery(id+"F0.wireOp",EDGE,"E13.3.0.0")}),1.0]])]});
            extrude(context, id + "F1", {"entities" : qUnion([Q0, Q1, Q2, Q3, Q4, Q5, Q6, Q7, Q8, Q9, Q10, Q11, Q12, Q13, Q14, Q15, Q16, Q17, Q18, Q19, Q20, Q21, Q22, Q23, Q24]), "oppositeDirection" : true, "depth" : 25 * mm, "hasSecondDirection" : true, "secondDirectionOppositeDirection" : true, "secondDirectionDepth" : 21 * mm});
        }
        {
            var Q0;
            Q0=makeQuery(id+"F1.opExtrude","SWEPT_BODY",BODY,{"disambiguationData":[OSD([sQuery(id+"F0.wireOp",EDGE,"E0.0"),sQuery(id+"F0.wireOp",EDGE,"E0.1"),sQuery(id+"F0.wireOp",EDGE,"E0.2"),sQuery(id+"F0.wireOp",EDGE,"E1.bottom"),sQuery(id+"F0.wireOp",EDGE,"E2.1.0.3"),sQuery(id+"F0.wireOp",EDGE,"E2.2.0.3"),sQuery(id+"F0.wireOp",EDGE,"E2.3.0.3"),sQuery(id+"F0.wireOp",EDGE,"E2.4.0.3"),sQuery(id+"F0.wireOp",EDGE,"E2.5.0.3"),sQuery(id+"F0.wireOp",EDGE,"E3.bottom"),sQuery(id+"F0.wireOp",EDGE,"E3.top"),sQuery(id+"F0.wireOp",EDGE,"E3.left"),sQuery(id+"F0.wireOp",EDGE,"E3.right"),sQuery(id+"F0.wireOp",EDGE,"E4.1.0.0"),sQuery(id+"F0.wireOp",EDGE,"E4.1.0.1"),sQuery(id+"F0.wireOp",EDGE,"E4.1.0.2"),sQuery(id+"F0.wireOp",EDGE,"E4.1.0.3"),sQuery(id+"F0.wireOp",EDGE,"E4.2.0.0"),sQuery(id+"F0.wireOp",EDGE,"E4.2.0.1"),sQuery(id+"F0.wireOp",EDGE,"E4.2.0.2"),sQuery(id+"F0.wireOp",EDGE,"E4.2.0.3"),sQuery(id+"F0.wireOp",EDGE,"E4.3.0.0"),sQuery(id+"F0.wireOp",EDGE,"E4.3.0.1"),sQuery(id+"F0.wireOp",EDGE,"E4.3.0.2"),sQuery(id+"F0.wireOp",EDGE,"E4.3.0.3"),sQuery(id+"F0.wireOp",EDGE,"E4.4.0.0"),sQuery(id+"F0.wireOp",EDGE,"E4.4.0.1"),sQuery(id+"F0.wireOp",EDGE,"E4.4.0.2"),sQuery(id+"F0.wireOp",EDGE,"E4.4.0.3"),sQuery(id+"F0.wireOp",EDGE,"E4.5.0.0"),sQuery(id+"F0.wireOp",EDGE,"E4.5.0.1"),sQuery(id+"F0.wireOp",EDGE,"E4.5.0.2"),sQuery(id+"F0.wireOp",EDGE,"E4.5.0.3"),sQuery(id+"F0.wireOp",EDGE,"E4.6.0.0"),sQuery(id+"F0.wireOp",EDGE,"E4.6.0.1"),sQuery(id+"F0.wireOp",EDGE,"E4.6.0.2"),sQuery(id+"F0.wireOp",EDGE,"E4.6.0.3"),sQuery(id+"F0.wireOp",EDGE,"E4.7.0.0"),sQuery(id+"F0.wireOp",EDGE,"E4.7.0.1"),sQuery(id+"F0.wireOp",EDGE,"E4.7.0.2"),sQuery(id+"F0.wireOp",EDGE,"E4.7.0.3"),sQuery(id+"F0.wireOp",EDGE,"KpDLyHw4-PIKC-jecU-MP4R-aqt8RiHXCLOJ"),sQuery(id+"F0.wireOp",EDGE,"l8Ocg7E3-WVaf-3syw-4Eul-Zz9p44A394Y8"),sQuery(id+"F0.wireOp",EDGE,"eQO8pUqr-jM6s-AsY3-pCeJ-34XryrRuDb6j"),sQuery(id+"F0.wireOp",EDGE,"cqxt34m7-r6yA-R2VF-Obax-9fo9XUA9Eafm"),sQuery(id+"F0.wireOp",EDGE,"5a172c00-1bc8-4c57-8483-bc0fd8c83645.1.0.0"),sQuery(id+"F0.wireOp",EDGE,"5a172c00-1bc8-4c57-8483-bc0fd8c83645.1.0.1"),sQuery(id+"F0.wireOp",EDGE,"5a172c00-1bc8-4c57-8483-bc0fd8c83645.1.0.2"),sQuery(id+"F0.wireOp",EDGE,"5a172c00-1bc8-4c57-8483-bc0fd8c83645.1.0.3"),sQuery(id+"F0.wireOp",EDGE,"5a172c00-1bc8-4c57-8483-bc0fd8c83645.2.0.0"),sQuery(id+"F0.wireOp",EDGE,"5a172c00-1bc8-4c57-8483-bc0fd8c83645.2.0.1"),sQuery(id+"F0.wireOp",EDGE,"5a172c00-1bc8-4c57-8483-bc0fd8c83645.2.0.2"),sQuery(id+"F0.wireOp",EDGE,"5a172c00-1bc8-4c57-8483-bc0fd8c83645.2.0.3"),sQuery(id+"F0.wireOp",EDGE,"5a172c00-1bc8-4c57-8483-bc0fd8c83645.3.0.0"),sQuery(id+"F0.wireOp",EDGE,"5a172c00-1bc8-4c57-8483-bc0fd8c83645.3.0.1"),sQuery(id+"F0.wireOp",EDGE,"5a172c00-1bc8-4c57-8483-bc0fd8c83645.3.0.2"),sQuery(id+"F0.wireOp",EDGE,"5a172c00-1bc8-4c57-8483-bc0fd8c83645.3.0.3"),sQuery(id+"F0.wireOp",EDGE,"5a172c00-1bc8-4c57-8483-bc0fd8c83645.4.0.0"),sQuery(id+"F0.wireOp",EDGE,"5a172c00-1bc8-4c57-8483-bc0fd8c83645.4.0.1"),sQuery(id+"F0.wireOp",EDGE,"5a172c00-1bc8-4c57-8483-bc0fd8c83645.4.0.2"),sQuery(id+"F0.wireOp",EDGE,"5a172c00-1bc8-4c57-8483-bc0fd8c83645.4.0.3"),sQuery(id+"F0.wireOp",EDGE,"5a172c00-1bc8-4c57-8483-bc0fd8c83645.5.0.0"),sQuery(id+"F0.wireOp",EDGE,"5a172c00-1bc8-4c57-8483-bc0fd8c83645.5.0.1"),sQuery(id+"F0.wireOp",EDGE,"5a172c00-1bc8-4c57-8483-bc0fd8c83645.5.0.2"),sQuery(id+"F0.wireOp",EDGE,"5a172c00-1bc8-4c57-8483-bc0fd8c83645.5.0.3"),sQuery(id+"F0.wireOp",EDGE,"5a172c00-1bc8-4c57-8483-bc0fd8c83645.6.0.0"),sQuery(id+"F0.wireOp",EDGE,"5a172c00-1bc8-4c57-8483-bc0fd8c83645.6.0.1"),sQuery(id+"F0.wireOp",EDGE,"5a172c00-1bc8-4c57-8483-bc0fd8c83645.6.0.2"),sQuery(id+"F0.wireOp",EDGE,"5a172c00-1bc8-4c57-8483-bc0fd8c83645.6.0.3"),sQuery(id+"F0.wireOp",EDGE,"5a172c00-1bc8-4c57-8483-bc0fd8c83645.7.0.0"),sQuery(id+"F0.wireOp",EDGE,"5a172c00-1bc8-4c57-8483-bc0fd8c83645.7.0.1"),sQuery(id+"F0.wireOp",EDGE,"5a172c00-1bc8-4c57-8483-bc0fd8c83645.7.0.2"),sQuery(id+"F0.wireOp",EDGE,"5a172c00-1bc8-4c57-8483-bc0fd8c83645.7.0.3"),sQuery(id+"F0.wireOp",EDGE,"5a172c00-1bc8-4c57-8483-bc0fd8c83645.8.0.0"),sQuery(id+"F0.wireOp",EDGE,"5a172c00-1bc8-4c57-8483-bc0fd8c83645.8.0.1"),sQuery(id+"F0.wireOp",EDGE,"5a172c00-1bc8-4c57-8483-bc0fd8c83645.8.0.2"),sQuery(id+"F0.wireOp",EDGE,"5a172c00-1bc8-4c57-8483-bc0fd8c83645.8.0.3"),sQuery(id+"F0.wireOp",EDGE,"5a172c00-1bc8-4c57-8483-bc0fd8c83645.9.0.0"),sQuery(id+"F0.wireOp",EDGE,"5a172c00-1bc8-4c57-8483-bc0fd8c83645.9.0.1"),sQuery(id+"F0.wireOp",EDGE,"5a172c00-1bc8-4c57-8483-bc0fd8c83645.9.0.2"),sQuery(id+"F0.wireOp",EDGE,"5a172c00-1bc8-4c57-8483-bc0fd8c83645.9.0.3"),sQuery(id+"F0.wireOp",EDGE,"156633df-8153-4ac4-959e-3bdcb70d4cf5.1.0.0"),sQuery(id+"F0.wireOp",EDGE,"156633df-8153-4ac4-959e-3bdcb70d4cf5.1.0.1"),sQuery(id+"F0.wireOp",EDGE,"156633df-8153-4ac4-959e-3bdcb70d4cf5.1.0.2"),sQuery(id+"F0.wireOp",EDGE,"156633df-8153-4ac4-959e-3bdcb70d4cf5.1.0.3"),sQuery(id+"F0.wireOp",EDGE,"dbb7825b-8b10-4ec2-b218-63f78ed2e39f0.MirrorCS"),sQuery(id+"F0.wireOp",EDGE,"575e46e0-75db-417e-8463-c8c3bb4939480.MirrorCS"),sQuery(id+"F0.wireOp",EDGE,"3236f841-74ef-4553-8bbd-e8b18ff503d60.MirrorCS"),sQuery(id+"F0.wireOp",EDGE,"c7b2fa67-672b-41f9-abb9-01b1d06c4ce80.MirrorCS"),sQuery(id+"F0.wireOp",EDGE,"72fe5725-794b-4cf3-8d93-636914991b0a0.MirrorCS"),sQuery(id+"F0.wireOp",EDGE,"1649282d-37e5-40d3-95bf-bd2a1584d9ca0.MirrorCS"),sQuery(id+"F0.wireOp",EDGE,"66e2f290-ecf6-45ff-86a5-976af37cd0680.MirrorCS"),sQuery(id+"F0.wireOp",EDGE,"4453aead-d696-4f96-84a8-33da7d01a6620.MirrorCS"),sQuery(id+"F0.wireOp",EDGE,"00cb52b6-8fd0-4997-a848-4b20b52a41290.MirrorCS"),sQuery(id+"F0.wireOp",EDGE,"ec6bc2f9-4d79-40fa-b474-217ebae306c20.MirrorCS"),sQuery(id+"F0.wireOp",EDGE,"e00b57c4-cf44-4c54-b5f3-03595547cf970.MirrorCS"),sQuery(id+"F0.wireOp",EDGE,"e3519527-86c6-4c60-82f2-78eba1c276a80.MirrorCS"),sQuery(id+"F0.wireOp",EDGE,"32b6c39d-5ec4-4ee6-a0f7-f2d71a5f72b90.MirrorCS"),sQuery(id+"F0.wireOp",EDGE,"d01a7970-0918-4dc2-a414-9f8a3eaa1c5a0.MirrorCS"),sQuery(id+"F0.wireOp",EDGE,"b03df699-8b32-4f68-b784-361de4daa5cf0.MirrorCS"),sQuery(id+"F0.wireOp",EDGE,"6d111b56-6417-4b74-95e0-27a2bd82cc720.MirrorCS"),sQuery(id+"F0.wireOp",EDGE,"1bef4a3e-6ba2-42b7-bc55-7ac99c6a8c160.MirrorCS"),sQuery(id+"F0.wireOp",EDGE,"ceb5d229-dc6f-44a9-b305-ae376306679b0.MirrorCS"),sQuery(id+"F0.wireOp",EDGE,"83c20e7f-f388-48e1-b39f-a7ff3bccd2e20.MirrorCS"),sQuery(id+"F0.wireOp",EDGE,"5629293e-866c-48b0-9c01-be2f40dc5c440.MirrorCS"),sQuery(id+"F0.wireOp",EDGE,"6c353f07-1bbe-4b02-b955-58c8f632309f0.MirrorCS"),sQuery(id+"F0.wireOp",EDGE,"08077180-c128-4338-9571-4a11e04edf380.MirrorCS"),sQuery(id+"F0.wireOp",EDGE,"82a63d79-4022-4da7-a0f1-a8947973e4df0.MirrorCS"),sQuery(id+"F0.wireOp",EDGE,"cf5789a1-f19e-422b-b5c8-9448f73a5aff0.MirrorCS"),sQuery(id+"F0.wireOp",EDGE,"707f1ed2-5dba-45ea-bd48-9eda4f5da48d0.MirrorCS"),sQuery(id+"F0.wireOp",EDGE,"ce8901be-c0f0-4103-ac93-0ebb9399d2680.MirrorCS"),sQuery(id+"F0.wireOp",EDGE,"09453591-1667-413a-9fd2-5439fa81007c0.MirrorCS"),sQuery(id+"F0.wireOp",EDGE,"4b5ef5aa-ee50-461d-8197-1a6894afa8290.MirrorCS"),sQuery(id+"F0.wireOp",EDGE,"f4632531-c8d3-4b5a-a34c-490049edd2c80.MirrorCS"),sQuery(id+"F0.wireOp",EDGE,"4e949b19-55a9-43e1-910e-d797c974a7450.MirrorCS"),sQuery(id+"F0.wireOp",EDGE,"e5ac3b62-e68b-40bc-a28d-32ea45c1ca8a0.MirrorCS"),sQuery(id+"F0.wireOp",EDGE,"be63ad97-70c8-41fe-9954-6ab768aa09680.MirrorCS"),sQuery(id+"F0.wireOp",EDGE,"2e110174-ce25-42ad-8f39-db498e464ccf0.MirrorCS"),sQuery(id+"F0.wireOp",EDGE,"99c68ed5-b90b-4ad9-bf66-afc926a4481b0.MirrorCS"),sQuery(id+"F0.wireOp",EDGE,"2ab78319-6a06-4c28-8e6c-8babfc0293a30.MirrorCS"),sQuery(id+"F0.wireOp",EDGE,"c785652f-a60c-4509-a2d1-a916b98ab1a20.MirrorCS"),sQuery(id+"F0.wireOp",EDGE,"8e5095ba-1890-4dbe-90dc-6cf65a5e8f0d0.MirrorCS"),sQuery(id+"F0.wireOp",EDGE,"89b2157f-245f-489d-af3c-205dc572d0350.MirrorCS"),sQuery(id+"F0.wireOp",EDGE,"27687945-7142-4b16-ac06-b3a62e1343200.MirrorCS"),sQuery(id+"F0.wireOp",EDGE,"7b96fb14-184b-4636-bba6-1427fedb13370.MirrorCS"),sQuery(id+"F0.wireOp",EDGE,"e12f4c84-2580-4bea-99e6-be72f3d822fd0.MirrorCS"),sQuery(id+"F0.wireOp",EDGE,"4ea93f6c-fe82-4207-ae63-27e6d9348e460.MirrorCS"),sQuery(id+"F0.wireOp",EDGE,"OwrMrZYV-yNjC-4na5-VGPR-d0a8jXyrihbf"),sQuery(id+"F0.wireOp",EDGE,"zwHntjTv-lkgw-YiWf-cdBR-gm1INsWGPLez")])]});
            var Q1;
            Q1=qCreatedBy(makeId("Top.planeOp"),FACE);
            mirror(context, id + "F2", {"entities" : qUnion([Q0]), "mirrorPlane" : qUnion([Q1])});
        }
        {
            var Q0;
            Q0=makeQuery(id+"FQspR15TdcOxWEM_1.splitOp","SPLIT",BODY,{"derivedFrom":makeQuery(id+"F2.opPattern","COPY",BODY,{"derivedFrom":makeQuery(id+"F1.opExtrude","SWEPT_BODY",BODY,{"disambiguationData":[OSD([sQuery(id+"F0.wireOp",EDGE,"E0.0"),sQuery(id+"F0.wireOp",EDGE,"E0.1"),sQuery(id+"F0.wireOp",EDGE,"E0.2"),sQuery(id+"F0.wireOp",EDGE,"E1.bottom"),sQuery(id+"F0.wireOp",EDGE,"E2.1.0.3"),sQuery(id+"F0.wireOp",EDGE,"E2.2.0.3"),sQuery(id+"F0.wireOp",EDGE,"E2.3.0.3"),sQuery(id+"F0.wireOp",EDGE,"E2.4.0.3"),sQuery(id+"F0.wireOp",EDGE,"E2.5.0.3"),sQuery(id+"F0.wireOp",EDGE,"E3.bottom"),sQuery(id+"F0.wireOp",EDGE,"E3.top"),sQuery(id+"F0.wireOp",EDGE,"E3.left"),sQuery(id+"F0.wireOp",EDGE,"E3.right"),sQuery(id+"F0.wireOp",EDGE,"E4.1.0.0"),sQuery(id+"F0.wireOp",EDGE,"E4.1.0.1"),sQuery(id+"F0.wireOp",EDGE,"E4.1.0.2"),sQuery(id+"F0.wireOp",EDGE,"E4.1.0.3"),sQuery(id+"F0.wireOp",EDGE,"E4.2.0.0"),sQuery(id+"F0.wireOp",EDGE,"E4.2.0.1"),sQuery(id+"F0.wireOp",EDGE,"E4.2.0.2"),sQuery(id+"F0.wireOp",EDGE,"E4.2.0.3"),sQuery(id+"F0.wireOp",EDGE,"E4.3.0.0"),sQuery(id+"F0.wireOp",EDGE,"E4.3.0.1"),sQuery(id+"F0.wireOp",EDGE,"E4.3.0.2"),sQuery(id+"F0.wireOp",EDGE,"E4.3.0.3"),sQuery(id+"F0.wireOp",EDGE,"E4.4.0.0"),sQuery(id+"F0.wireOp",EDGE,"E4.4.0.1"),sQuery(id+"F0.wireOp",EDGE,"E4.4.0.2"),sQuery(id+"F0.wireOp",EDGE,"E4.4.0.3"),sQuery(id+"F0.wireOp",EDGE,"E4.5.0.0"),sQuery(id+"F0.wireOp",EDGE,"E4.5.0.1"),sQuery(id+"F0.wireOp",EDGE,"E4.5.0.2"),sQuery(id+"F0.wireOp",EDGE,"E4.5.0.3"),sQuery(id+"F0.wireOp",EDGE,"E4.6.0.0"),sQuery(id+"F0.wireOp",EDGE,"E4.6.0.1"),sQuery(id+"F0.wireOp",EDGE,"E4.6.0.2"),sQuery(id+"F0.wireOp",EDGE,"E4.6.0.3"),sQuery(id+"F0.wireOp",EDGE,"E4.7.0.0"),sQuery(id+"F0.wireOp",EDGE,"E4.7.0.1"),sQuery(id+"F0.wireOp",EDGE,"E4.7.0.2"),sQuery(id+"F0.wireOp",EDGE,"E4.7.0.3"),sQuery(id+"F0.wireOp",EDGE,"KpDLyHw4-PIKC-jecU-MP4R-aqt8RiHXCLOJ"),sQuery(id+"F0.wireOp",EDGE,"l8Ocg7E3-WVaf-3syw-4Eul-Zz9p44A394Y8"),sQuery(id+"F0.wireOp",EDGE,"eQO8pUqr-jM6s-AsY3-pCeJ-34XryrRuDb6j"),sQuery(id+"F0.wireOp",EDGE,"cqxt34m7-r6yA-R2VF-Obax-9fo9XUA9Eafm"),sQuery(id+"F0.wireOp",EDGE,"5a172c00-1bc8-4c57-8483-bc0fd8c83645.1.0.0"),sQuery(id+"F0.wireOp",EDGE,"5a172c00-1bc8-4c57-8483-bc0fd8c83645.1.0.1"),sQuery(id+"F0.wireOp",EDGE,"5a172c00-1bc8-4c57-8483-bc0fd8c83645.1.0.2"),sQuery(id+"F0.wireOp",EDGE,"5a172c00-1bc8-4c57-8483-bc0fd8c83645.1.0.3"),sQuery(id+"F0.wireOp",EDGE,"5a172c00-1bc8-4c57-8483-bc0fd8c83645.2.0.0"),sQuery(id+"F0.wireOp",EDGE,"5a172c00-1bc8-4c57-8483-bc0fd8c83645.2.0.1"),sQuery(id+"F0.wireOp",EDGE,"5a172c00-1bc8-4c57-8483-bc0fd8c83645.2.0.2"),sQuery(id+"F0.wireOp",EDGE,"5a172c00-1bc8-4c57-8483-bc0fd8c83645.2.0.3"),sQuery(id+"F0.wireOp",EDGE,"5a172c00-1bc8-4c57-8483-bc0fd8c83645.3.0.0"),sQuery(id+"F0.wireOp",EDGE,"5a172c00-1bc8-4c57-8483-bc0fd8c83645.3.0.1"),sQuery(id+"F0.wireOp",EDGE,"5a172c00-1bc8-4c57-8483-bc0fd8c83645.3.0.2"),sQuery(id+"F0.wireOp",EDGE,"5a172c00-1bc8-4c57-8483-bc0fd8c83645.3.0.3"),sQuery(id+"F0.wireOp",EDGE,"5a172c00-1bc8-4c57-8483-bc0fd8c83645.4.0.0"),sQuery(id+"F0.wireOp",EDGE,"5a172c00-1bc8-4c57-8483-bc0fd8c83645.4.0.1"),sQuery(id+"F0.wireOp",EDGE,"5a172c00-1bc8-4c57-8483-bc0fd8c83645.4.0.2"),sQuery(id+"F0.wireOp",EDGE,"5a172c00-1bc8-4c57-8483-bc0fd8c83645.4.0.3"),sQuery(id+"F0.wireOp",EDGE,"5a172c00-1bc8-4c57-8483-bc0fd8c83645.5.0.0"),sQuery(id+"F0.wireOp",EDGE,"5a172c00-1bc8-4c57-8483-bc0fd8c83645.5.0.1"),sQuery(id+"F0.wireOp",EDGE,"5a172c00-1bc8-4c57-8483-bc0fd8c83645.5.0.2"),sQuery(id+"F0.wireOp",EDGE,"5a172c00-1bc8-4c57-8483-bc0fd8c83645.5.0.3"),sQuery(id+"F0.wireOp",EDGE,"5a172c00-1bc8-4c57-8483-bc0fd8c83645.6.0.0"),sQuery(id+"F0.wireOp",EDGE,"5a172c00-1bc8-4c57-8483-bc0fd8c83645.6.0.1"),sQuery(id+"F0.wireOp",EDGE,"5a172c00-1bc8-4c57-8483-bc0fd8c83645.6.0.2"),sQuery(id+"F0.wireOp",EDGE,"5a172c00-1bc8-4c57-8483-bc0fd8c83645.6.0.3"),sQuery(id+"F0.wireOp",EDGE,"5a172c00-1bc8-4c57-8483-bc0fd8c83645.7.0.0"),sQuery(id+"F0.wireOp",EDGE,"5a172c00-1bc8-4c57-8483-bc0fd8c83645.7.0.1"),sQuery(id+"F0.wireOp",EDGE,"5a172c00-1bc8-4c57-8483-bc0fd8c83645.7.0.2"),sQuery(id+"F0.wireOp",EDGE,"5a172c00-1bc8-4c57-8483-bc0fd8c83645.7.0.3"),sQuery(id+"F0.wireOp",EDGE,"5a172c00-1bc8-4c57-8483-bc0fd8c83645.8.0.0"),sQuery(id+"F0.wireOp",EDGE,"5a172c00-1bc8-4c57-8483-bc0fd8c83645.8.0.1"),sQuery(id+"F0.wireOp",EDGE,"5a172c00-1bc8-4c57-8483-bc0fd8c83645.8.0.2"),sQuery(id+"F0.wireOp",EDGE,"5a172c00-1bc8-4c57-8483-bc0fd8c83645.8.0.3"),sQuery(id+"F0.wireOp",EDGE,"5a172c00-1bc8-4c57-8483-bc0fd8c83645.9.0.0"),sQuery(id+"F0.wireOp",EDGE,"5a172c00-1bc8-4c57-8483-bc0fd8c83645.9.0.1"),sQuery(id+"F0.wireOp",EDGE,"5a172c00-1bc8-4c57-8483-bc0fd8c83645.9.0.2"),sQuery(id+"F0.wireOp",EDGE,"5a172c00-1bc8-4c57-8483-bc0fd8c83645.9.0.3"),sQuery(id+"F0.wireOp",EDGE,"156633df-8153-4ac4-959e-3bdcb70d4cf5.1.0.0"),sQuery(id+"F0.wireOp",EDGE,"156633df-8153-4ac4-959e-3bdcb70d4cf5.1.0.1"),sQuery(id+"F0.wireOp",EDGE,"156633df-8153-4ac4-959e-3bdcb70d4cf5.1.0.2"),sQuery(id+"F0.wireOp",EDGE,"156633df-8153-4ac4-959e-3bdcb70d4cf5.1.0.3"),sQuery(id+"F0.wireOp",EDGE,"dbb7825b-8b10-4ec2-b218-63f78ed2e39f0.MirrorCS"),sQuery(id+"F0.wireOp",EDGE,"575e46e0-75db-417e-8463-c8c3bb4939480.MirrorCS"),sQuery(id+"F0.wireOp",EDGE,"3236f841-74ef-4553-8bbd-e8b18ff503d60.MirrorCS"),sQuery(id+"F0.wireOp",EDGE,"c7b2fa67-672b-41f9-abb9-01b1d06c4ce80.MirrorCS"),sQuery(id+"F0.wireOp",EDGE,"72fe5725-794b-4cf3-8d93-636914991b0a0.MirrorCS"),sQuery(id+"F0.wireOp",EDGE,"1649282d-37e5-40d3-95bf-bd2a1584d9ca0.MirrorCS"),sQuery(id+"F0.wireOp",EDGE,"66e2f290-ecf6-45ff-86a5-976af37cd0680.MirrorCS"),sQuery(id+"F0.wireOp",EDGE,"4453aead-d696-4f96-84a8-33da7d01a6620.MirrorCS"),sQuery(id+"F0.wireOp",EDGE,"00cb52b6-8fd0-4997-a848-4b20b52a41290.MirrorCS"),sQuery(id+"F0.wireOp",EDGE,"ec6bc2f9-4d79-40fa-b474-217ebae306c20.MirrorCS"),sQuery(id+"F0.wireOp",EDGE,"e00b57c4-cf44-4c54-b5f3-03595547cf970.MirrorCS"),sQuery(id+"F0.wireOp",EDGE,"e3519527-86c6-4c60-82f2-78eba1c276a80.MirrorCS"),sQuery(id+"F0.wireOp",EDGE,"32b6c39d-5ec4-4ee6-a0f7-f2d71a5f72b90.MirrorCS"),sQuery(id+"F0.wireOp",EDGE,"d01a7970-0918-4dc2-a414-9f8a3eaa1c5a0.MirrorCS"),sQuery(id+"F0.wireOp",EDGE,"b03df699-8b32-4f68-b784-361de4daa5cf0.MirrorCS"),sQuery(id+"F0.wireOp",EDGE,"6d111b56-6417-4b74-95e0-27a2bd82cc720.MirrorCS"),sQuery(id+"F0.wireOp",EDGE,"1bef4a3e-6ba2-42b7-bc55-7ac99c6a8c160.MirrorCS"),sQuery(id+"F0.wireOp",EDGE,"ceb5d229-dc6f-44a9-b305-ae376306679b0.MirrorCS"),sQuery(id+"F0.wireOp",EDGE,"83c20e7f-f388-48e1-b39f-a7ff3bccd2e20.MirrorCS"),sQuery(id+"F0.wireOp",EDGE,"5629293e-866c-48b0-9c01-be2f40dc5c440.MirrorCS"),sQuery(id+"F0.wireOp",EDGE,"6c353f07-1bbe-4b02-b955-58c8f632309f0.MirrorCS"),sQuery(id+"F0.wireOp",EDGE,"08077180-c128-4338-9571-4a11e04edf380.MirrorCS"),sQuery(id+"F0.wireOp",EDGE,"82a63d79-4022-4da7-a0f1-a8947973e4df0.MirrorCS"),sQuery(id+"F0.wireOp",EDGE,"cf5789a1-f19e-422b-b5c8-9448f73a5aff0.MirrorCS"),sQuery(id+"F0.wireOp",EDGE,"707f1ed2-5dba-45ea-bd48-9eda4f5da48d0.MirrorCS"),sQuery(id+"F0.wireOp",EDGE,"ce8901be-c0f0-4103-ac93-0ebb9399d2680.MirrorCS"),sQuery(id+"F0.wireOp",EDGE,"09453591-1667-413a-9fd2-5439fa81007c0.MirrorCS"),sQuery(id+"F0.wireOp",EDGE,"4b5ef5aa-ee50-461d-8197-1a6894afa8290.MirrorCS"),sQuery(id+"F0.wireOp",EDGE,"f4632531-c8d3-4b5a-a34c-490049edd2c80.MirrorCS"),sQuery(id+"F0.wireOp",EDGE,"4e949b19-55a9-43e1-910e-d797c974a7450.MirrorCS"),sQuery(id+"F0.wireOp",EDGE,"e5ac3b62-e68b-40bc-a28d-32ea45c1ca8a0.MirrorCS"),sQuery(id+"F0.wireOp",EDGE,"be63ad97-70c8-41fe-9954-6ab768aa09680.MirrorCS"),sQuery(id+"F0.wireOp",EDGE,"2e110174-ce25-42ad-8f39-db498e464ccf0.MirrorCS"),sQuery(id+"F0.wireOp",EDGE,"99c68ed5-b90b-4ad9-bf66-afc926a4481b0.MirrorCS"),sQuery(id+"F0.wireOp",EDGE,"2ab78319-6a06-4c28-8e6c-8babfc0293a30.MirrorCS"),sQuery(id+"F0.wireOp",EDGE,"c785652f-a60c-4509-a2d1-a916b98ab1a20.MirrorCS"),sQuery(id+"F0.wireOp",EDGE,"8e5095ba-1890-4dbe-90dc-6cf65a5e8f0d0.MirrorCS"),sQuery(id+"F0.wireOp",EDGE,"89b2157f-245f-489d-af3c-205dc572d0350.MirrorCS"),sQuery(id+"F0.wireOp",EDGE,"OwrMrZYV-yNjC-4na5-VGPR-d0a8jXyrihbf"),sQuery(id+"F0.wireOp",EDGE,"zwHntjTv-lkgw-YiWf-cdBR-gm1INsWGPLez"),sQuery(id+"F0.wireOp",EDGE,"b8fb8cb9-396d-4aa3-a288-f28caeffbab2.1.0.0"),sQuery(id+"F0.wireOp",EDGE,"b8fb8cb9-396d-4aa3-a288-f28caeffbab2.1.0.1"),sQuery(id+"F0.wireOp",EDGE,"b8fb8cb9-396d-4aa3-a288-f28caeffbab2.1.0.2"),sQuery(id+"F0.wireOp",EDGE,"b8fb8cb9-396d-4aa3-a288-f28caeffbab2.1.0.3")])]}),"instanceName":"1"}),"isFromBackBody":true});
            deleteBodies(context, id + "F3", {"entities" : qUnion([Q0])});
        }
        {
            var Q0;
            {var subQ0=sQuery(id+"F0.wireOp",EDGE,"E17.MirrorCS");Q0=makeQuery(id+"F0.imprint","IMPRINT",FACE,{"disambiguationData":[TD([[makeQuery(id+"F0.imprint","IMPRINT",EDGE,{"derivedFrom":subQ0}),1.0]])]});}
            var Q1;
            {var subQ0=sQuery(id+"F0.wireOp",EDGE,"E33.MirrorCS");var subQ1=sQuery(id+"F0.wireOp",EDGE,"E19.MirrorCS");var subQ2=makeQuery(id+"F0.imprint","INTERSECT",VERTEX,{"derivedFrom":[subQ1,subQ0]});Q1=makeQuery(id+"F0.imprint","IMPRINT",FACE,{"disambiguationData":[TD([[makeQuery(id+"F0.imprint","IMPRINT",EDGE,{"disambiguationData":[TD([[subQ2,-1.0]])],"derivedFrom":subQ1}),1.0]])]});}
            var Q2;
            {var subQ0=sQuery(id+"F0.wireOp",EDGE,"E33.MirrorCS");var subQ1=sQuery(id+"F0.wireOp",EDGE,"E22.MirrorCS");var subQ2=makeQuery(id+"F0.imprint","INTERSECT",VERTEX,{"derivedFrom":[subQ1,subQ0]});Q2=makeQuery(id+"F0.imprint","IMPRINT",FACE,{"disambiguationData":[TD([[makeQuery(id+"F0.imprint","IMPRINT",EDGE,{"disambiguationData":[TD([[subQ2,-1.0]])],"derivedFrom":subQ1}),1.0]])]});}
            var Q3;
            {var subQ0=sQuery(id+"F0.wireOp",EDGE,"E33.MirrorCS");var subQ1=sQuery(id+"F0.wireOp",EDGE,"E26.MirrorCS");var subQ2=makeQuery(id+"F0.imprint","INTERSECT",VERTEX,{"derivedFrom":[subQ1,subQ0]});Q3=makeQuery(id+"F0.imprint","IMPRINT",FACE,{"disambiguationData":[TD([[makeQuery(id+"F0.imprint","IMPRINT",EDGE,{"disambiguationData":[TD([[subQ2,-1.0]])],"derivedFrom":subQ1}),1.0]])]});}
            var Q4;
            {var subQ0=sQuery(id+"F0.wireOp",EDGE,"E33.MirrorCS");var subQ1=sQuery(id+"F0.wireOp",EDGE,"E30.MirrorCS");var subQ2=makeQuery(id+"F0.imprint","INTERSECT",VERTEX,{"derivedFrom":[subQ1,subQ0]});Q4=makeQuery(id+"F0.imprint","IMPRINT",FACE,{"disambiguationData":[TD([[makeQuery(id+"F0.imprint","IMPRINT",EDGE,{"disambiguationData":[TD([[subQ2,-1.0]])],"derivedFrom":subQ1}),1.0]])]});}
            var Q5;
            {var subQ0=sQuery(id+"F0.wireOp",EDGE,"E37.MirrorCS");Q5=makeQuery(id+"F0.imprint","IMPRINT",FACE,{"disambiguationData":[TD([[makeQuery(id+"F0.imprint","IMPRINT",EDGE,{"derivedFrom":subQ0}),1.0]])]});}
            var Q6;
            {var subQ0=sQuery(id+"F0.wireOp",EDGE,"E41.MirrorCS");Q6=makeQuery(id+"F0.imprint","IMPRINT",FACE,{"disambiguationData":[TD([[makeQuery(id+"F0.imprint","IMPRINT",EDGE,{"derivedFrom":subQ0}),1.0]])]});}
            var Q7;
            {var subQ0=sQuery(id+"F0.wireOp",EDGE,"E44.MirrorCS");Q7=makeQuery(id+"F0.imprint","IMPRINT",FACE,{"disambiguationData":[TD([[makeQuery(id+"F0.imprint","IMPRINT",EDGE,{"derivedFrom":subQ0}),1.0]])]});}
            var Q8;
            {var subQ0=sQuery(id+"F0.wireOp",EDGE,"E51.MirrorCS");Q8=makeQuery(id+"F0.imprint","IMPRINT",FACE,{"disambiguationData":[TD([[makeQuery(id+"F0.imprint","IMPRINT",EDGE,{"derivedFrom":subQ0}),1.0]])]});}
            var Q9;
            {var subQ0=sQuery(id+"F0.wireOp",EDGE,"E52.MirrorCS");Q9=makeQuery(id+"F0.imprint","IMPRINT",FACE,{"disambiguationData":[TD([[makeQuery(id+"F0.imprint","IMPRINT",EDGE,{"derivedFrom":subQ0}),1.0]])]});}
            var Q10;
            {var subQ0=sQuery(id+"F0.wireOp",EDGE,"E56.MirrorCS");Q10=makeQuery(id+"F0.imprint","IMPRINT",FACE,{"disambiguationData":[TD([[makeQuery(id+"F0.imprint","IMPRINT",EDGE,{"derivedFrom":subQ0}),1.0]])]});}
            var Q11;
            {var subQ0=sQuery(id+"F0.wireOp",EDGE,"E60.MirrorCS");Q11=makeQuery(id+"F0.imprint","IMPRINT",FACE,{"disambiguationData":[TD([[makeQuery(id+"F0.imprint","IMPRINT",EDGE,{"derivedFrom":subQ0}),1.0]])]});}
            var Q12;
            {var subQ0=sQuery(id+"F0.wireOp",EDGE,"E64.MirrorCS");Q12=makeQuery(id+"F0.imprint","IMPRINT",FACE,{"disambiguationData":[TD([[makeQuery(id+"F0.imprint","IMPRINT",EDGE,{"derivedFrom":subQ0}),1.0]])]});}
            var Q13;
            {var subQ0=sQuery(id+"F0.wireOp",EDGE,"E68.MirrorCS");Q13=makeQuery(id+"F0.imprint","IMPRINT",FACE,{"disambiguationData":[TD([[makeQuery(id+"F0.imprint","IMPRINT",EDGE,{"derivedFrom":subQ0}),1.0]])]});}
            var Q14;
            {var subQ0=sQuery(id+"F0.wireOp",EDGE,"E72.MirrorCS");Q14=makeQuery(id+"F0.imprint","IMPRINT",FACE,{"disambiguationData":[TD([[makeQuery(id+"F0.imprint","IMPRINT",EDGE,{"derivedFrom":subQ0}),1.0]])]});}
            var Q15;
            Q15=makeQuery(id+"F0.imprint","IMPRINT",FACE,{"disambiguationData":[TD([[makeQuery(id+"F0.imprint","IMPRINT",EDGE,{"derivedFrom":sQuery(id+"F0.wireOp",EDGE,"E74.MirrorCS")}),1.0]])]});
            var Q16;
            Q16=makeQuery(id+"F0.imprint","IMPRINT",FACE,{"disambiguationData":[TD([[makeQuery(id+"F0.imprint","IMPRINT",EDGE,{"derivedFrom":sQuery(id+"F0.wireOp",EDGE,"E78.MirrorCS")}),1.0]])]});
            var Q17;
            Q17=makeQuery(id+"F0.imprint","IMPRINT",FACE,{"disambiguationData":[TD([[makeQuery(id+"F0.imprint","IMPRINT",EDGE,{"derivedFrom":sQuery(id+"F0.wireOp",EDGE,"E82.MirrorCS")}),1.0]])]});
            var Q18;
            {var subQ0=sQuery(id+"F0.wireOp",EDGE,"E86.MirrorCS");Q18=makeQuery(id+"F0.imprint","IMPRINT",FACE,{"disambiguationData":[TD([[makeQuery(id+"F0.imprint","IMPRINT",EDGE,{"derivedFrom":subQ0}),1.0]])]});}
            extrude(context, id + "F4", {"entities" : qUnion([Q0, Q1, Q2, Q3, Q4, Q5, Q6, Q7, Q8, Q9, Q10, Q11, Q12, Q13, Q14, Q15, Q16, Q17, Q18]), "oppositeDirection" : true, "depth" : 25 * mm, "hasSecondDirection" : true, "secondDirectionOppositeDirection" : false, "secondDirectionDepth" : 29 * mm});
        }
        {
            var Q0;
            {var subQ22=sQuery(id+"F0.wireOp",EDGE,"E6.3.0.1");Q0=makeQuery(id+"F0.imprint","IMPRINT",FACE,{"disambiguationData":[TD([[makeQuery(id+"F0.imprint","IMPRINT",EDGE,{"derivedFrom":subQ22}),-1.0]])]});}
            extrude(context, id + "F5", {"entities" : qUnion([Q0]), "depth" : 25 * mm, "hasSecondDirection" : true, "secondDirectionOppositeDirection" : true, "secondDirectionDepth" : 21 * mm});
        }
        {
            var Q0;
            {var subQ0=sQuery(id+"F0.wireOp",EDGE,"E105");var subQ1=sQuery(id+"F0.wireOp",EDGE,"E28.MirrorCS");var subQ2=makeQuery(id+"F0.imprint","INTERSECT",VERTEX,{"derivedFrom":[subQ1,subQ0]});Q0=makeQuery(id+"F0.imprint","IMPRINT",FACE,{"disambiguationData":[TD([[makeQuery(id+"F0.imprint","IMPRINT",EDGE,{"disambiguationData":[TD([[subQ2,-1.0]])],"derivedFrom":subQ1}),-1.0]])]});}
            var Q1;
            {var subQ0=sQuery(id+"F0.wireOp",EDGE,"E105");var subQ1=sQuery(id+"F0.wireOp",EDGE,"E24.MirrorCS");var subQ2=makeQuery(id+"F0.imprint","INTERSECT",VERTEX,{"derivedFrom":[subQ1,subQ0]});Q1=makeQuery(id+"F0.imprint","IMPRINT",FACE,{"disambiguationData":[TD([[makeQuery(id+"F0.imprint","IMPRINT",EDGE,{"disambiguationData":[TD([[subQ2,-1.0]])],"derivedFrom":subQ1}),-1.0]])]});}
            var Q2;
            {var subQ0=sQuery(id+"F0.wireOp",EDGE,"E105");var subQ1=sQuery(id+"F0.wireOp",EDGE,"E21.MirrorCS");var subQ2=makeQuery(id+"F0.imprint","INTERSECT",VERTEX,{"derivedFrom":[subQ1,subQ0]});Q2=makeQuery(id+"F0.imprint","IMPRINT",FACE,{"disambiguationData":[TD([[makeQuery(id+"F0.imprint","IMPRINT",EDGE,{"disambiguationData":[TD([[subQ2,-1.0]])],"derivedFrom":subQ1}),-1.0]])]});}
            var Q3;
            {var subQ0=sQuery(id+"F0.wireOp",EDGE,"E17.MirrorCS");Q3=makeQuery(id+"F0.imprint","IMPRINT",FACE,{"disambiguationData":[TD([[makeQuery(id+"F0.imprint","IMPRINT",EDGE,{"derivedFrom":subQ0}),-1.0]])]});}
            var Q4;
            Q4=makeQuery(id+"F0.imprint","IMPRINT",FACE,{"disambiguationData":[TD([[makeQuery(id+"F0.imprint","IMPRINT",EDGE,{"derivedFrom":sQuery(id+"F0.wireOp",EDGE,"E13.9.0.0")}),1.0]])]});
            extrude(context, id + "F6", {"entities" : qUnion([Q0, Q1, Q2, Q3, Q4]), "depth" : 25 * mm, "hasSecondDirection" : true, "secondDirectionOppositeDirection" : true, "secondDirectionDepth" : 21 * mm});
        }
    });
